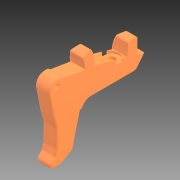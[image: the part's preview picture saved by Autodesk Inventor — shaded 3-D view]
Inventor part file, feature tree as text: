
AUTODESK INVENTOR PART (.ipt)
format: ipt  version: 2020 (Build 240168000, 168)  size: 891,904 bytes
history: native  units: in
note: dims shown in document units (in); Inventor stores cm internally (conversion verified against a paired STEP export)
features: extrude x13, sketch x13, fillet x5, plane x2, projected_geometry x2, revolve x1, chamfer x1, imported_body x1
ambient origin geometry x8: Origin, YZ Plane, XZ Plane, XY Plane, X Axis, Y Axis, Z Axis, Center Point
bodies: Solid1 (feature_tree)
feature tree (38):
  extrude  "Extrusion1"  Depth=0.3937in TaperAngle=0.0deg
  extrude  "Extrusion2"  Depth=0.5906in
  extrude  "Extrusion3"  TaperAngle=90.0deg  [1 undecoded]
  revolve  "Revolution1"  [1 undecoded]
  extrude  "Extrusion4"  TaperAngle=0.0deg  [1 undecoded]
  extrude  "Extrusion5"  Depth=0.1181in
  extrude  "Extrusion6"  TaperAngle=0.0deg  [1 undecoded]
  extrude  "Extrusion8"  TaperAngle=0.0deg  [1 undecoded]
  fillet  "Fillet2"  Radius=0.0394in
  fillet  "Fillet4"  Radius=0.0394in
  sketch  "Sketch11"  dims[d50=0.1969in d51=0.1969in]
  extrude  "Extrusion10"  Depth=0.1969in
  extrude  "Extrusion14"  Depth=2.9528in
  extrude  "Extrusion11"  Depth=0.0787in TaperAngle=0.0deg
  plane  "Work Plane3"
  plane  "Work Plane4"
  extrude  "Extrusion15"  Depth=0.0394in TaperAngle=0.0deg
  extrude  "Extrusion16"  Depth=0.3937in TaperAngle=0.0deg
  fillet  "Fillet9"  Radius=0.1378in
  fillet  "Fillet10"  Radius=0.3937in
  extrude  "Extrusion17"  Depth=0.0295in
  chamfer  "Chamfer4"  Distance=0.0394in
  fillet  "Fillet11"  Radius=0.0295in
  sketch  "Sketch1"  dims[d0=0.0in d1=0.0in d2=0.3937in d3=0.0in]
  sketch  "Sketch2"  dims[d4=0.1969in d5=0.5906in]
  sketch  "Sketch3"  dims[d6=0.0787in d7=90.0deg]
  sketch  "Sketch4"  dims[d8=0.1575in d9=0.315in]
  sketch  "Sketch5"  dims[d10=0.0787in d11=0.0in d12=0.0in d13=0.0in]
  sketch  "Sketch6"  dims[d14=0.0481in d15=0.1181in]
  sketch  "Sketch7"  dims[d16=0.7874in d17=0.0in d18=0.0in]
  sketch  "Sketch9"  dims[d19=0.0in d20=0.0in d32=0.0in d33=0.0in d34=0.0394in d36=0.0394in]
  sketch  "Sketch12"  dims[d52=1.1811in d53=2.9528in]
  projected_geometry  "Projected Loop1"
  sketch  "Sketch15"  dims[d55=0.1718in d56=15.0deg d59=0.0787in d60=0.0in]
  sketch  "Sketch16"  dims[d61=0.0295in d62=0.0in d71=0.0394in d72=0.0in]
  sketch  "Sketch17"  dims[d73=0.1378in d74=0.3937in d75=0.0in d76=0.1378in d77=0.3937in d78=0.0in d79=0.0295in d80=0.0394in d81=0.0295in d82=0.0in d83=0.4921in d84=0.3937in d85=0.0394in d86=0.0787in d87=45.0deg d88=0.0394in]
  projected_geometry  "Projected Loop2"
  imported_body  "Base1"
note: 5 required parameter values undecoded (feature->parameter linkage not recoverable at this tier; creation-order binding heuristic only, values carry confidence <= 0.55)